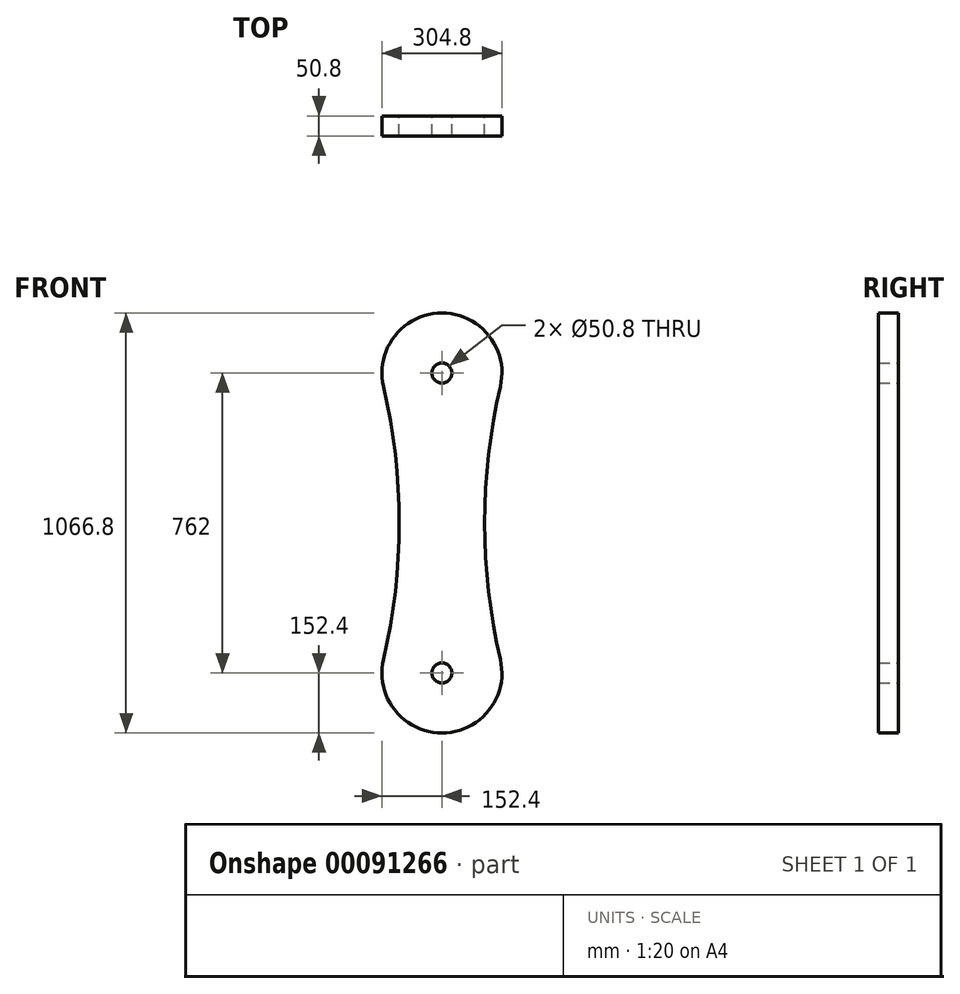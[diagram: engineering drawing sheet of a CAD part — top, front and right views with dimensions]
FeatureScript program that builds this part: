
annotation { "Feature Type Name" : "Feature", "Feature Type Description" : "" }
export const myFeature = defineFeature(function(context is Context, id is Id, definition is map)
    precondition{}
    {
        {
            var Q0;
            Q0=qCreatedBy(makeId("Front.planeOp"),FACE);
            var sketch = newSketch(context, id + "F0", { "sketchPlane" : qUnion([Q0])});
            skArc(sketch, "E0", {"start": v(-148.41, 34.64) * mm, "mid": v(0, -152.4) * mm, "end": v(148.41, 34.64) * mm});
            skArc(sketch, "E1", {"start": v(148.41, 727.36) * mm, "mid": v(0, 914.4) * mm, "end": v(-148.41, 727.36) * mm});
            skArc(sketch, "E2", {"start": v(-148.41, 34.64) * mm, "mid": v(-108.53, 381) * mm, "end": v(-148.41, 727.36) * mm});
            skCircle(sketch, "E3", {"center": v(0, 0) * mm, "radius": 25.4 * mm});
            skCircle(sketch, "E4", {"center": v(0, 762) * mm, "radius": 25.4 * mm});
            skArc(sketch, "E5", {"start": v(148.41, 727.36) * mm, "mid": v(108.53, 381) * mm, "end": v(148.41, 34.64) * mm});
            skSolve(sketch);
        }
        {
            var Q0;
            Q0=makeQuery(id+"F0.imprint","IMPRINT",FACE,{"disambiguationData":[TD([[makeQuery(id+"F0.imprint","IMPRINT",EDGE,{"derivedFrom":sQuery(id+"F0.wireOp",EDGE,"E0")}),1.0]])]});
            extrude(context, id + "F1", {"entities" : qUnion([Q0]), "depth" : 50.8 * mm});
        }
    });
